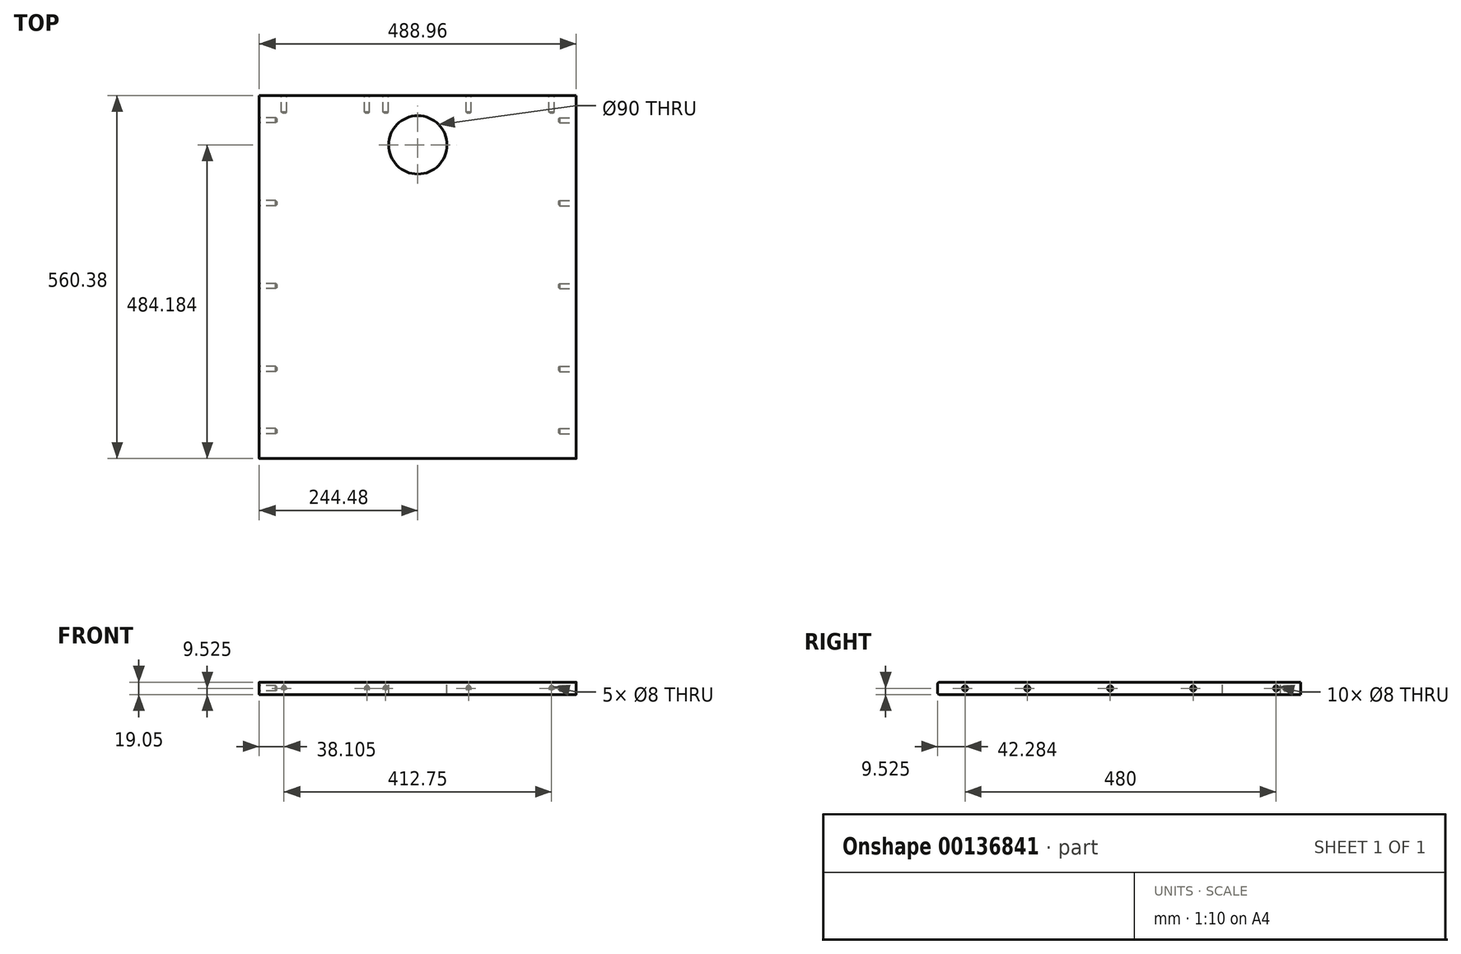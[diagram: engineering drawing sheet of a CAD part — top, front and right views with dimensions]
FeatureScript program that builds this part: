
annotation { "Feature Type Name" : "Feature", "Feature Type Description" : "" }
export const myFeature = defineFeature(function(context is Context, id is Id, definition is map)
    precondition{}
    {
        {
            var Q0;
            Q0=qCreatedBy(makeId("Top.planeOp"),FACE);
            var sketch = newSketch(context, id + "F0", { "sketchPlane" : qUnion([Q0])});
            skLineSegment(sketch, "E0.bottom", {"start": v(244.48, -280.2) * mm, "end": v(-244.47, -280.2) * mm});
            skLineSegment(sketch, "E0.top", {"start": v(244.47, 280.2) * mm, "end": v(-244.48, 280.2) * mm});
            skLineSegment(sketch, "E0.left", {"start": v(244.48, -280.2) * mm, "end": v(244.47, 280.2) * mm});
            skLineSegment(sketch, "E0.right", {"start": v(-244.47, -280.2) * mm, "end": v(-244.48, 280.2) * mm});
            skPoint(sketch, "E0.middle", {"position": v(0, 0) * mm});
            skSolve(sketch);
        }
        {
            var Q0;
            Q0=makeQuery(id+"F0.imprint","IMPRINT",FACE,{"disambiguationData":[TD([[makeQuery(id+"F0.imprint","IMPRINT",EDGE,{"derivedFrom":sQuery(id+"F0.wireOp",EDGE,"E0.bottom")}),-1.0]])]});
            extrude(context, id + "F1", {"entities" : qUnion([Q0]), "oppositeDirection" : true, "depth" : 19.05 * mm});
        }
        {
            var Q0;
            Q0=makeQuery(id+"F1.opExtrude","SWEPT_FACE",FACE,{"disambiguationData":[OSD([sQuery(id+"F0.wireOp",EDGE,"E0.left")])]});
            var sketch = newSketch(context, id + "F2", { "sketchPlane" : qUnion([Q0])});
            skPoint(sketch, "E1", {"position": v(242.1, -9.53) * mm});
            skPoint(sketch, "E2", {"position": v(114.1, -9.53) * mm});
            skPoint(sketch, "E3", {"position": v(-13.9, -9.53) * mm});
            skPoint(sketch, "E4", {"position": v(-141.9, -9.53) * mm});
            skPoint(sketch, "E5", {"position": v(-237.9, -9.53) * mm});
            skSolve(sketch);
        }
        {
            var Q0;
            Q0=qCreatedBy(makeId("Right.planeOp"),FACE);
            var sketch = newSketch(context, id + "F3", { "sketchPlane" : qUnion([Q0])});
            skPoint(sketch, "E6", {"position": v(-271.83, -132.34) * mm});
            skCircle(sketch, "E7", {"center": v(-271.83, -132.34) * mm, "radius": 4 * mm});
            skSolve(sketch);
        }
        {
            var Q0;
            Q0=makeQuery(id+"F3.imprint","IMPRINT",FACE,{"disambiguationData":[TD([[makeQuery(id+"F3.imprint","IMPRINT",EDGE,{"derivedFrom":sQuery(id+"F3.wireOp",EDGE,"E7")}),1.0]])]});
            extrude(context, id + "F4", {"entities" : qUnion([Q0]), "oppositeDirection" : true, "depth" : 26.99 * mm});
        }
        {
            var Q0;
            Q0=makeQuery(id+"F4.opExtrude","CAP_EDGE",EDGE,{"disambiguationData":[OSD([sQuery(id+"F3.wireOp",EDGE,"E7")])],"isStart":false});
            chamfer(context, id + "F5", {"entities" : qUnion([Q0]), "width" : 1.59 * mm, "tangentPropagation" : true});
        }
        {
            var Q0;
            Q0=makeQuery(id+"F4.opExtrude","SWEPT_BODY",BODY,{"disambiguationData":[OSD([sQuery(id+"F3.wireOp",EDGE,"E7")])]});
            var Q1;
            Q1=sQuery(id+"F3.wireOp",VERTEX,"E6");
            var Q2;
            Q2=sQuery(id+"F2.wireOp",VERTEX,"E5");
            transform(context, id + "F6", {"entities" : qUnion([Q0]), "transformType" : TransformType.TRANSLATION_ENTITY, "oppositeDirectionEntity" : false, "transformLine" : qUnion([Q1, Q2]), "makeCopy" : true});
        }
        {
            var Q0;
            Q0=makeQuery(id+"F4.opExtrude","SWEPT_BODY",BODY,{"disambiguationData":[OSD([sQuery(id+"F3.wireOp",EDGE,"E7")])]});
            var Q1;
            Q1=sQuery(id+"F3.wireOp",VERTEX,"E6");
            var Q2;
            Q2=sQuery(id+"F2.wireOp",VERTEX,"E4");
            transform(context, id + "F7", {"entities" : qUnion([Q0]), "transformType" : TransformType.TRANSLATION_ENTITY, "oppositeDirectionEntity" : false, "transformLine" : qUnion([Q1, Q2]), "makeCopy" : true});
        }
        {
            var Q0;
            Q0=makeQuery(id+"F4.opExtrude","SWEPT_BODY",BODY,{"disambiguationData":[OSD([sQuery(id+"F3.wireOp",EDGE,"E7")])]});
            var Q1;
            Q1=sQuery(id+"F3.wireOp",VERTEX,"E6");
            var Q2;
            Q2=sQuery(id+"F2.wireOp",VERTEX,"E3");
            transform(context, id + "F8", {"entities" : qUnion([Q0]), "transformType" : TransformType.TRANSLATION_ENTITY, "oppositeDirectionEntity" : false, "transformLine" : qUnion([Q1, Q2]), "makeCopy" : true});
        }
        {
            var Q0;
            Q0=makeQuery(id+"F4.opExtrude","SWEPT_BODY",BODY,{"disambiguationData":[OSD([sQuery(id+"F3.wireOp",EDGE,"E7")])]});
            var Q1;
            Q1=sQuery(id+"F3.wireOp",VERTEX,"E6");
            var Q2;
            Q2=sQuery(id+"F2.wireOp",VERTEX,"E2");
            transform(context, id + "F9", {"entities" : qUnion([Q0]), "transformType" : TransformType.TRANSLATION_ENTITY, "oppositeDirectionEntity" : false, "transformLine" : qUnion([Q1, Q2]), "makeCopy" : true});
        }
        {
            var Q0;
            Q0=makeQuery(id+"F4.opExtrude","SWEPT_BODY",BODY,{"disambiguationData":[OSD([sQuery(id+"F3.wireOp",EDGE,"E7")])]});
            var Q1;
            Q1=sQuery(id+"F3.wireOp",VERTEX,"E6");
            var Q2;
            Q2=sQuery(id+"F2.wireOp",VERTEX,"E1");
            transform(context, id + "F10", {"entities" : qUnion([Q0]), "transformType" : TransformType.TRANSLATION_ENTITY, "oppositeDirectionEntity" : false, "transformLine" : qUnion([Q1, Q2]), "makeCopy" : true});
        }
        {
            var Q0;
            Q0=makeQuery(id+"F6.opPattern","COPY",BODY,{"derivedFrom":makeQuery(id+"F4.opExtrude","SWEPT_BODY",BODY,{"disambiguationData":[OSD([sQuery(id+"F3.wireOp",EDGE,"E7")])]}),"instanceName":"1"});
            var Q1;
            Q1=makeQuery(id+"F7.opPattern","COPY",BODY,{"derivedFrom":makeQuery(id+"F4.opExtrude","SWEPT_BODY",BODY,{"disambiguationData":[OSD([sQuery(id+"F3.wireOp",EDGE,"E7")])]}),"instanceName":"1"});
            var Q2;
            Q2=makeQuery(id+"F8.opPattern","COPY",BODY,{"derivedFrom":makeQuery(id+"F4.opExtrude","SWEPT_BODY",BODY,{"disambiguationData":[OSD([sQuery(id+"F3.wireOp",EDGE,"E7")])]}),"instanceName":"1"});
            var Q3;
            Q3=makeQuery(id+"F9.opPattern","COPY",BODY,{"derivedFrom":makeQuery(id+"F4.opExtrude","SWEPT_BODY",BODY,{"disambiguationData":[OSD([sQuery(id+"F3.wireOp",EDGE,"E7")])]}),"instanceName":"1"});
            var Q4;
            Q4=makeQuery(id+"F10.opPattern","COPY",BODY,{"derivedFrom":makeQuery(id+"F4.opExtrude","SWEPT_BODY",BODY,{"disambiguationData":[OSD([sQuery(id+"F3.wireOp",EDGE,"E7")])]}),"instanceName":"1"});
            var Q5;
            Q5=qCreatedBy(makeId("Right.planeOp"),FACE);
            mirror(context, id + "F11", {"entities" : qUnion([Q0, Q1, Q2, Q3, Q4]), "mirrorPlane" : qUnion([Q5])});
        }
        {
            var Q0;
            Q0=makeQuery(id+"F11.opPattern","COPY",BODY,{"derivedFrom":makeQuery(id+"F6.opPattern","COPY",BODY,{"derivedFrom":makeQuery(id+"F4.opExtrude","SWEPT_BODY",BODY,{"disambiguationData":[OSD([sQuery(id+"F3.wireOp",EDGE,"E7")])]}),"instanceName":"1"}),"instanceName":"1"});
            var Q1;
            Q1=makeQuery(id+"F11.opPattern","COPY",BODY,{"derivedFrom":makeQuery(id+"F7.opPattern","COPY",BODY,{"derivedFrom":makeQuery(id+"F4.opExtrude","SWEPT_BODY",BODY,{"disambiguationData":[OSD([sQuery(id+"F3.wireOp",EDGE,"E7")])]}),"instanceName":"1"}),"instanceName":"1"});
            var Q2;
            Q2=makeQuery(id+"F11.opPattern","COPY",BODY,{"derivedFrom":makeQuery(id+"F8.opPattern","COPY",BODY,{"derivedFrom":makeQuery(id+"F4.opExtrude","SWEPT_BODY",BODY,{"disambiguationData":[OSD([sQuery(id+"F3.wireOp",EDGE,"E7")])]}),"instanceName":"1"}),"instanceName":"1"});
            var Q3;
            Q3=makeQuery(id+"F11.opPattern","COPY",BODY,{"derivedFrom":makeQuery(id+"F9.opPattern","COPY",BODY,{"derivedFrom":makeQuery(id+"F4.opExtrude","SWEPT_BODY",BODY,{"disambiguationData":[OSD([sQuery(id+"F3.wireOp",EDGE,"E7")])]}),"instanceName":"1"}),"instanceName":"1"});
            var Q4;
            Q4=makeQuery(id+"F11.opPattern","COPY",BODY,{"derivedFrom":makeQuery(id+"F10.opPattern","COPY",BODY,{"derivedFrom":makeQuery(id+"F4.opExtrude","SWEPT_BODY",BODY,{"disambiguationData":[OSD([sQuery(id+"F3.wireOp",EDGE,"E7")])]}),"instanceName":"1"}),"instanceName":"1"});
            var Q5;
            Q5=makeQuery(id+"F10.opPattern","COPY",BODY,{"derivedFrom":makeQuery(id+"F4.opExtrude","SWEPT_BODY",BODY,{"disambiguationData":[OSD([sQuery(id+"F3.wireOp",EDGE,"E7")])]}),"instanceName":"1"});
            var Q6;
            Q6=makeQuery(id+"F9.opPattern","COPY",BODY,{"derivedFrom":makeQuery(id+"F4.opExtrude","SWEPT_BODY",BODY,{"disambiguationData":[OSD([sQuery(id+"F3.wireOp",EDGE,"E7")])]}),"instanceName":"1"});
            var Q7;
            Q7=makeQuery(id+"F8.opPattern","COPY",BODY,{"derivedFrom":makeQuery(id+"F4.opExtrude","SWEPT_BODY",BODY,{"disambiguationData":[OSD([sQuery(id+"F3.wireOp",EDGE,"E7")])]}),"instanceName":"1"});
            var Q8;
            Q8=makeQuery(id+"F7.opPattern","COPY",BODY,{"derivedFrom":makeQuery(id+"F4.opExtrude","SWEPT_BODY",BODY,{"disambiguationData":[OSD([sQuery(id+"F3.wireOp",EDGE,"E7")])]}),"instanceName":"1"});
            var Q9;
            Q9=makeQuery(id+"F6.opPattern","COPY",BODY,{"derivedFrom":makeQuery(id+"F4.opExtrude","SWEPT_BODY",BODY,{"disambiguationData":[OSD([sQuery(id+"F3.wireOp",EDGE,"E7")])]}),"instanceName":"1"});
            var Q10;
            Q10=makeQuery(id+"F1.opExtrude","SWEPT_BODY",BODY,{"disambiguationData":[OSD([sQuery(id+"F0.wireOp",EDGE,"E0.bottom"),sQuery(id+"F0.wireOp",EDGE,"E0.top"),sQuery(id+"F0.wireOp",EDGE,"E0.left"),sQuery(id+"F0.wireOp",EDGE,"E0.right")])]});
            booleanBodies(context, id + "F12", {"operationType" : BooleanOperationType.SUBTRACTION, "tools" : qUnion([Q0, Q1, Q2, Q3, Q4, Q5, Q6, Q7, Q8, Q9]), "targets" : qUnion([Q10])});
        }
        {
            var Q0;
            Q0=makeQuery(id+"F4.opExtrude","SWEPT_BODY",BODY,{"disambiguationData":[OSD([sQuery(id+"F3.wireOp",EDGE,"E7")])]});
            var Q1;
            Q1=makeQuery(id+"F1.opExtrude","SWEPT_EDGE",EDGE,{"disambiguationData":[OSD([sQuery(id+"F0.wireOp",EDGE,"E0.bottom"),sQuery(id+"F0.wireOp",EDGE,"E0.left")])]});
            transform(context, id + "F13", {"entities" : qUnion([Q0]), "transformType" : TransformType.ROTATION, "transformAxis" : qUnion([Q1]), "angle" : 90 * degree, "makeCopy" : false});
        }
        {
            var Q0;
            Q0=makeQuery(id+"F4.opExtrude","CAP_FACE",FACE,{"disambiguationData":[OSD([sQuery(id+"F3.wireOp",EDGE,"E7")])],"isStart":true});
            var sketch = newSketch(context, id + "F14", { "sketchPlane" : qUnion([Q0])});
            skPoint(sketch, "E8", {"position": v(-236.1, -132.34) * mm});
            skSolve(sketch);
        }
        {
            var Q0;
            Q0=makeQuery(id+"F1.opExtrude","SWEPT_FACE",FACE,{"disambiguationData":[OSD([sQuery(id+"F0.wireOp",EDGE,"E0.top")])]});
            var sketch = newSketch(context, id + "F15", { "sketchPlane" : qUnion([Q0])});
            skPoint(sketch, "E9", {"position": v(-206.38, -9.53) * mm});
            skPoint(sketch, "E10", {"position": v(-78.38, -9.53) * mm});
            skPoint(sketch, "E11", {"position": v(49.62, -9.53) * mm});
            skPoint(sketch, "E12", {"position": v(78.38, -9.53) * mm});
            skPoint(sketch, "E13", {"position": v(206.38, -9.53) * mm});
            skSolve(sketch);
        }
        {
            var Q0;
            Q0=makeQuery(id+"F4.opExtrude","SWEPT_BODY",BODY,{"disambiguationData":[OSD([sQuery(id+"F3.wireOp",EDGE,"E7")])]});
            var Q1;
            Q1=sQuery(id+"F14.wireOp",VERTEX,"E8");
            var Q2;
            Q2=sQuery(id+"F15.wireOp",VERTEX,"E13");
            transform(context, id + "F16", {"entities" : qUnion([Q0]), "transformType" : TransformType.TRANSLATION_ENTITY, "oppositeDirectionEntity" : false, "transformLine" : qUnion([Q1, Q2]), "makeCopy" : true});
        }
        {
            var Q0;
            Q0=makeQuery(id+"F4.opExtrude","SWEPT_BODY",BODY,{"disambiguationData":[OSD([sQuery(id+"F3.wireOp",EDGE,"E7")])]});
            var Q1;
            Q1=sQuery(id+"F14.wireOp",VERTEX,"E8");
            var Q2;
            Q2=sQuery(id+"F15.wireOp",VERTEX,"E12");
            transform(context, id + "F17", {"entities" : qUnion([Q0]), "transformType" : TransformType.TRANSLATION_ENTITY, "oppositeDirectionEntity" : false, "transformLine" : qUnion([Q1, Q2]), "makeCopy" : true});
        }
        {
            var Q0;
            Q0=makeQuery(id+"F4.opExtrude","SWEPT_BODY",BODY,{"disambiguationData":[OSD([sQuery(id+"F3.wireOp",EDGE,"E7")])]});
            var Q1;
            Q1=sQuery(id+"F14.wireOp",VERTEX,"E8");
            var Q2;
            Q2=sQuery(id+"F15.wireOp",VERTEX,"E11");
            transform(context, id + "F18", {"entities" : qUnion([Q0]), "transformType" : TransformType.TRANSLATION_ENTITY, "oppositeDirectionEntity" : false, "transformLine" : qUnion([Q1, Q2]), "makeCopy" : true});
        }
        {
            var Q0;
            Q0=makeQuery(id+"F4.opExtrude","SWEPT_BODY",BODY,{"disambiguationData":[OSD([sQuery(id+"F3.wireOp",EDGE,"E7")])]});
            var Q1;
            Q1=sQuery(id+"F14.wireOp",VERTEX,"E8");
            var Q2;
            Q2=sQuery(id+"F15.wireOp",VERTEX,"E10");
            transform(context, id + "F19", {"entities" : qUnion([Q0]), "transformType" : TransformType.TRANSLATION_ENTITY, "oppositeDirectionEntity" : false, "transformLine" : qUnion([Q1, Q2]), "makeCopy" : true});
        }
        {
            var Q0;
            Q0=makeQuery(id+"F4.opExtrude","SWEPT_BODY",BODY,{"disambiguationData":[OSD([sQuery(id+"F3.wireOp",EDGE,"E7")])]});
            var Q1;
            Q1=sQuery(id+"F14.wireOp",VERTEX,"E8");
            var Q2;
            Q2=sQuery(id+"F15.wireOp",VERTEX,"E9");
            transform(context, id + "F20", {"entities" : qUnion([Q0]), "transformType" : TransformType.TRANSLATION_ENTITY, "oppositeDirectionEntity" : false, "transformLine" : qUnion([Q1, Q2]), "makeCopy" : false});
        }
        {
            var Q0;
            Q0=makeQuery(id+"F16.opPattern","COPY",BODY,{"derivedFrom":makeQuery(id+"F4.opExtrude","SWEPT_BODY",BODY,{"disambiguationData":[OSD([sQuery(id+"F3.wireOp",EDGE,"E7")])]}),"instanceName":"1"});
            var Q1;
            Q1=makeQuery(id+"F17.opPattern","COPY",BODY,{"derivedFrom":makeQuery(id+"F4.opExtrude","SWEPT_BODY",BODY,{"disambiguationData":[OSD([sQuery(id+"F3.wireOp",EDGE,"E7")])]}),"instanceName":"1"});
            var Q2;
            Q2=makeQuery(id+"F18.opPattern","COPY",BODY,{"derivedFrom":makeQuery(id+"F4.opExtrude","SWEPT_BODY",BODY,{"disambiguationData":[OSD([sQuery(id+"F3.wireOp",EDGE,"E7")])]}),"instanceName":"1"});
            var Q3;
            Q3=makeQuery(id+"F19.opPattern","COPY",BODY,{"derivedFrom":makeQuery(id+"F4.opExtrude","SWEPT_BODY",BODY,{"disambiguationData":[OSD([sQuery(id+"F3.wireOp",EDGE,"E7")])]}),"instanceName":"1"});
            var Q4;
            Q4=makeQuery(id+"F4.opExtrude","SWEPT_BODY",BODY,{"disambiguationData":[OSD([sQuery(id+"F3.wireOp",EDGE,"E7")])]});
            var Q5;
            Q5=makeQuery(id+"F1.opExtrude","SWEPT_BODY",BODY,{"disambiguationData":[OSD([sQuery(id+"F0.wireOp",EDGE,"E0.bottom"),sQuery(id+"F0.wireOp",EDGE,"E0.top"),sQuery(id+"F0.wireOp",EDGE,"E0.left"),sQuery(id+"F0.wireOp",EDGE,"E0.right")])]});
            booleanBodies(context, id + "F21", {"operationType" : BooleanOperationType.SUBTRACTION, "tools" : qUnion([Q0, Q1, Q2, Q3, Q4]), "targets" : qUnion([Q5])});
        }
        {
            var Q0;
            Q0=makeQuery(id+"F1.opExtrude","CAP_EDGE",EDGE,{"disambiguationData":[OSD([sQuery(id+"F0.wireOp",EDGE,"E0.bottom")])],"isStart":false});
            var Q1;
            Q1=makeQuery(id+"F1.opExtrude","CAP_EDGE",EDGE,{"disambiguationData":[OSD([sQuery(id+"F0.wireOp",EDGE,"E0.bottom")])],"isStart":true});
            fillet(context, id + "F22", {"entities" : qUnion([Q0, Q1]), "radius" : 3.17 * mm, "tangentPropagation" : true, "allowEdgeOverflow" : false});
        }
        {
            var Q0;
            Q0=makeQuery(id+"F1.opExtrude","CAP_FACE",FACE,{"disambiguationData":[OSD([sQuery(id+"F0.wireOp",EDGE,"E0.bottom"),sQuery(id+"F0.wireOp",EDGE,"E0.top"),sQuery(id+"F0.wireOp",EDGE,"E0.left"),sQuery(id+"F0.wireOp",EDGE,"E0.right")])],"isStart":true});
            var sketch = newSketch(context, id + "F23", { "sketchPlane" : qUnion([Q0])});
            skCircle(sketch, "E14", {"center": v(0, 204) * mm, "radius": 45 * mm});
            skSolve(sketch);
        }
        {
            var Q0;
            Q0=makeQuery(id+"F23.imprint","IMPRINT",FACE,{"disambiguationData":[TD([[makeQuery(id+"F23.imprint","IMPRINT",EDGE,{"derivedFrom":sQuery(id+"F23.wireOp",EDGE,"E14")}),1.0]])]});
            extrude(context, id + "F24", {"entities" : qUnion([Q0]), "operationType" : NewBodyOperationType.REMOVE, "endBound" : BoundingType.THROUGH_ALL, "oppositeDirection" : true, "depth" : 25.4 * mm});
        }
    });
